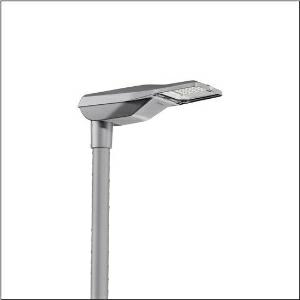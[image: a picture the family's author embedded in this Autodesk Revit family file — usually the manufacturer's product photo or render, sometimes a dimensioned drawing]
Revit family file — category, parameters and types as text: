
# Revit family: streetlight_sl_21_iq_micro___p0_8a_5xe1u31g08cb_6469
name_source: partatom
category: Lighting Fixtures
units: mm (PartAtom-declared; Revit-internal decimal feet)

## family parameters
Cut with Voids When Loaded = No
Host = Face
Light Source = No
Part Type = Normal
Room Calculation Point = No
Round Connector Dimension = Use Diameter
Shared = No

## types (1)
- --- (1 x LED, 2830 lm, 19.4 W, 3000K)
    Apparent Load = 19 VA
    CIE Flux Codes = 33 69 96 100 100
    Color Rendering = 70
    Color Temperature = 3000K
    Default Elevation = 1800 mm
    Description = Streetlight SL 21 iQ micro, mast luminaire, primary light control with lens, of PMMA, primary optical cover: cover, of toughened safety glass, transparent, light distribution: P0.8a, light emission: direct distribution, primary light characteristic: asymmetric, installation type: post-top, side-entry, LED, High Power LED, rated luminous flux: 2.830lm, luminous efficacy: 146lm/W, light colour: 730, colour temperature: 3000K, control gear: iQ Street-Remote, control: pre-setting: linear dimming characteristic, Street-Remote, Auto-Match, Temp-Guard, Lumen-Switch, Night-Set, Smart-Wire, Light-Fading, Desk-Remote (wireless, voltage-free reading and setting of iQ features in the workshop via application-optimized NFC function/RFID function), optimised constant luminous flux control (CLO 2.0), mains connection: 220..240V, AC, 50/60Hz, start of lifetime: 19W, end of service life: 20W, reduction: 10W, luminaire housing, of diecast aluminium, powder-coated, SITECO metallic grey (DB 702S), corrosivity category C5 high according to DIN EN ISO 12944, please order mast flange separately, inclination adjustable: 0°, 5°, 10°, 15°, sealing non-destructively replaceable, multi-level sealing system, length: 528mm, width: 235mm, height: 110mm, mast flange for spigot size: 42mm (side-entry): 5XC10008XM4, 60/48mm (side-entry/post-top): 5XC10108XM2, 76/60mm (side-entry/post-top): 5XC10108XM1, protection rating (complete): IP66, insulation class (complete): insulation class II (safety insulation), certification: CE, ENEC, ENEC+, VDE, impact resistance: IK10, permissible operating ambient temperature for outdoor applications: -40..+50°C, standard-compliant lighting for roads and squares, packaging unit: 1 piece

Light Distribution: P0.8a
    Height = 110 mm
    Lamp = 1 x LED
    Lamp Light Flux = 2830 lm
    Lamp Power = 19.4 W
    Lamp count = 1
    Length = 528 mm
    Luminous efficacy = 146 lm/W
    Manufacturer = Siteco
    ModVariant = No
    Model = 5XE1U31G08CB
    Number of Poles = 1
    OnlyDefault = Yes
    Power Factor = 1
    Product Name = Streetlight SL 21 iQ micro | P0.8a
    Product group = mast luminaire | pylon top
    ProductGroupID = 6100
    Protection Class = Protection class II
    Protection Degree = IP 66
    RLX_Detail_Level = 1
    RLX_Emergency_Light_Flux = 0 lm
    RLX_Emergency_Type = 0
    RLX_Emergency_Type_DB = No
    RlxData = <blob elided: 98789 chars, md5=84749e75>
    Socket = socket
    Standby Power = 0 W
    System Light Flux = 2830 lm
    System Power = 19 W
    Type Comments = factory setting: luminous flux: 100 % | dim-lin: 254 | 387 mA
    Type Image = l_1006881.jpg
    URL = http://relux.com
    VarID = @adj_080745
    Voltage = 0 V
    Weight = 0.00 kg
    Width = 235 mm

## geometry (parser evidence)
native form markers: Blend x4, Sweep x10
no freeform markers — native parametric forms only
